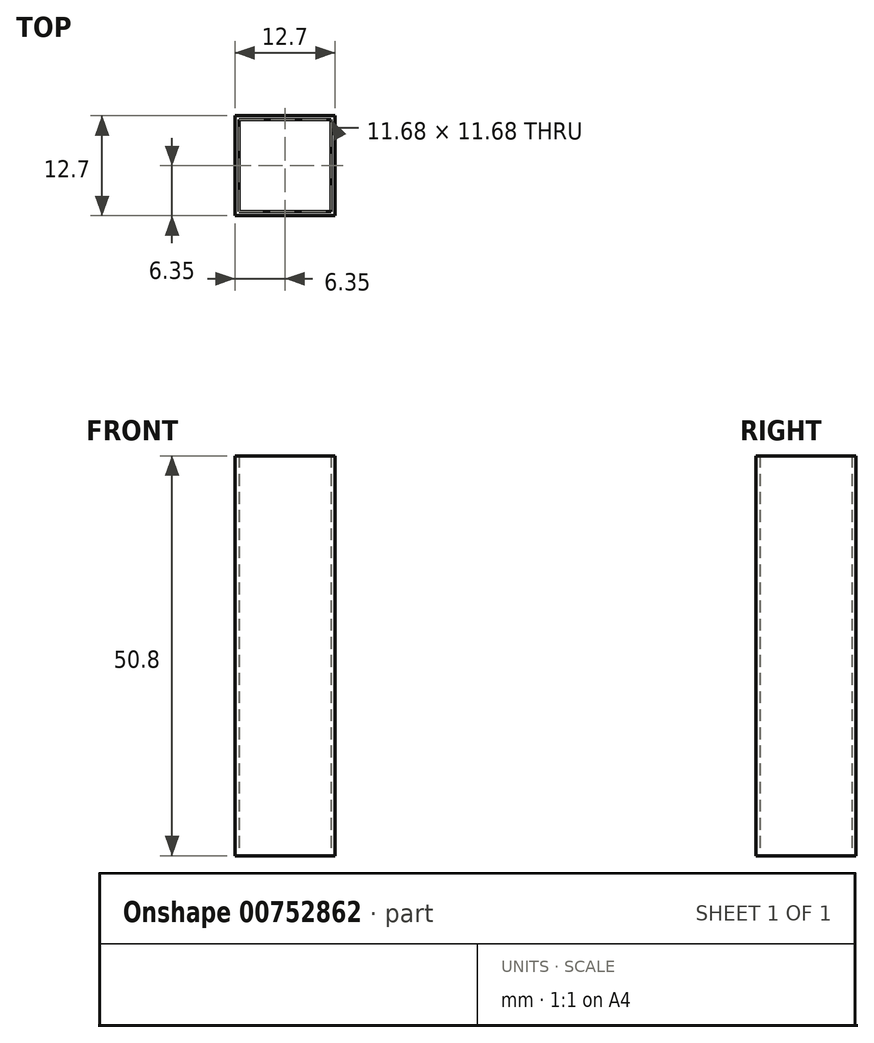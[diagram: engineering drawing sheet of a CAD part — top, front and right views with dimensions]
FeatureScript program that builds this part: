
annotation { "Feature Type Name" : "Feature", "Feature Type Description" : "" }
export const myFeature = defineFeature(function(context is Context, id is Id, definition is map)
    precondition{}
    {
        {
            var Q0;
            Q0=qCreatedBy(makeId("Top.planeOp"),FACE);
            var sketch = newSketch(context, id + "F0", { "sketchPlane" : qUnion([Q0])});
            skLineSegment(sketch, "E0.bottom", {"start": v(6.35, 6.35) * mm, "end": v(-6.35, 6.35) * mm});
            skLineSegment(sketch, "E0.top", {"start": v(6.35, -6.35) * mm, "end": v(-6.35, -6.35) * mm});
            skLineSegment(sketch, "E0.left", {"start": v(6.35, 6.35) * mm, "end": v(6.35, -6.35) * mm});
            skLineSegment(sketch, "E0.right", {"start": v(-6.35, 6.35) * mm, "end": v(-6.35, -6.35) * mm});
            skPoint(sketch, "E0.middle", {"position": v(0, 0) * mm});
            skLineSegment(sketch, "E1.bottom", {"start": v(5.84, -5.84) * mm, "end": v(-5.84, -5.84) * mm});
            skLineSegment(sketch, "E1.top", {"start": v(5.84, 5.84) * mm, "end": v(-5.84, 5.84) * mm});
            skLineSegment(sketch, "E1.left", {"start": v(5.84, -5.84) * mm, "end": v(5.84, 5.84) * mm});
            skLineSegment(sketch, "E1.right", {"start": v(-5.84, -5.84) * mm, "end": v(-5.84, 5.84) * mm});
            skSolve(sketch);
        }
        {
            var Q0;
            Q0=makeQuery(id+"F0.imprint","IMPRINT",FACE,{"disambiguationData":[TD([[makeQuery(id+"F0.imprint","IMPRINT",EDGE,{"derivedFrom":sQuery(id+"F0.wireOp",EDGE,"E0.bottom")}),1.0]])]});
            extrude(context, id + "F1", {"entities" : qUnion([Q0]), "depth" : 50.8 * mm, "offsetDistance" : 25.4 * mm});
        }
    });
